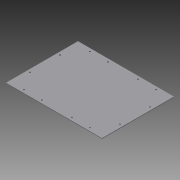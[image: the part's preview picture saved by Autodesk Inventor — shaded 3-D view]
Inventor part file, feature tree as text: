
AUTODESK INVENTOR PART (.ipt)
format: ipt  version: 2015 (Build 190159000, 159)  size: 121,856 bytes
history: native  units: in
note: dims shown in document units (in); Inventor stores cm internally (conversion verified against a paired STEP export)
features: extrude x2, sketch x2
ambient origin geometry x8: Origin, YZ Plane, XZ Plane, XY Plane, X Axis, Y Axis, Z Axis, Center Point
bodies: Solid1 (feature_tree)
feature tree (4):
  extrude  "Extrusion1"  Depth=6.0in
  extrude  "Extrusion2"  Depth=6.0in
  sketch  "Sketch1"  dims[d0=8.0in d1=6.0in]
  sketch  "Sketch3"  dims[d2=0.05in d3=0.0in d36=0.125in d37=0.125in d38=0.125in d39=0.125in d40=0.125in d41=0.125in d42=0.125in d43=0.125in d45=0.25in d46=1.75in d47=0.25in d48=1.25in d49=1.25in d50=0.25in d51=1.75in d52=0.25in d53=1.75in d54=0.25in d55=1.25in d56=0.25in d57=1.25in d58=0.2499in d59=1.75in d60=1.0in d61=0.0in d62=8.0in d63=6.0in d64=2.75in d65=0.125in d66=0.25in d67=2.75in d68=0.125in d69=0.25in d70=0.125in d71=0.25in d72=2.75in d73=0.125in d74=0.25in d75=2.75in]
